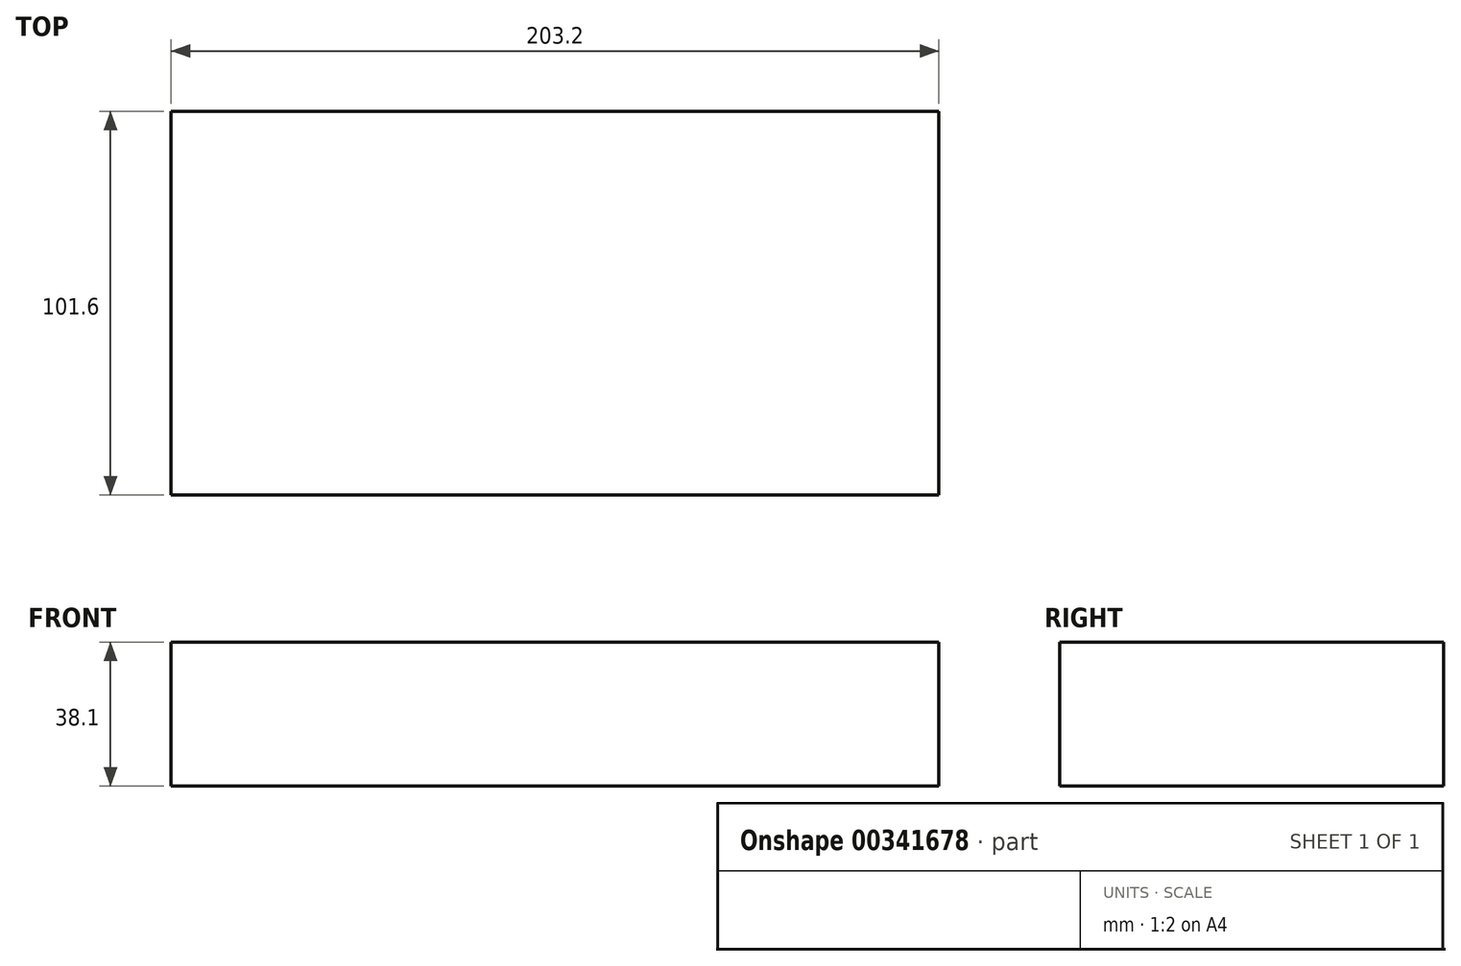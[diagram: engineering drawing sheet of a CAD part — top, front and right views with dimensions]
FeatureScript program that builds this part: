
annotation { "Feature Type Name" : "Feature", "Feature Type Description" : "" }
export const myFeature = defineFeature(function(context is Context, id is Id, definition is map)
    precondition{}
    {
        {
            var Q0;
            Q0=qCreatedBy(makeId("Front.planeOp"),FACE);
            var sketch = newSketch(context, id + "F0", { "sketchPlane" : qUnion([Q0])});
            skLineSegment(sketch, "E0.bottom", {"start": v(-158.68, 30.26) * mm, "end": v(44.52, 30.26) * mm});
            skLineSegment(sketch, "E0.top", {"start": v(-158.68, -7.84) * mm, "end": v(44.52, -7.84) * mm});
            skLineSegment(sketch, "E0.left", {"start": v(-158.68, 30.26) * mm, "end": v(-158.68, -7.84) * mm});
            skLineSegment(sketch, "E0.right", {"start": v(44.52, 30.26) * mm, "end": v(44.52, -7.84) * mm});
            skSolve(sketch);
        }
        {
            var Q0;
            Q0=makeQuery(id+"F0.imprint","IMPRINT",FACE,{"disambiguationData":[TD([[makeQuery(id+"F0.imprint","IMPRINT",EDGE,{"derivedFrom":sQuery(id+"F0.wireOp",EDGE,"E0.bottom")}),-1.0]])]});
            extrude(context, id + "F1", {"entities" : qUnion([Q0]), "depth" : 101.6 * mm, "offsetDistance" : 25.4 * mm});
        }
    });
